FCSTD DOCUMENT  (FreeCAD 0.20R29410 (Git))
Label: co2-sensor-case-v3
License: All rights reserved
LicenseURL: http://en.wikipedia.org/wiki/All_rights_reserved
objects: Part::Extrusion×10, Sketcher::SketchObject×7, Part::Cut×2, Part::Fillet×2, PartDesign::FeatureBase×1, PartDesign::Pocket×1, PartDesign::PolarPattern×1, PartDesign::Body×1, Part::FeaturePython×1
note: 27 computed .brp shape members not serialized (recipe doc carries the construction recipe); baked Part::Feature solids carry a one-line shape summary decoded from their .brp

FEATURE [Sketcher::SketchObject] Sketch
  FullyConstrained = true
  MapMode = 5
  Support = -> [XY_Plane]
  sketch-geometry (2):
    g0: Circle CenterX=0 CenterY=0 CenterZ=0 NormalX=0 NormalY=0 NormalZ=1 AngleXU=0 Radius=20
    g1: Circle CenterX=0 CenterY=0 CenterZ=0 NormalX=0 NormalY=0 NormalZ=1 AngleXU=0 Radius=18
  constraints (4):
    c: Coincident(g0,g-1)
    c: Diameter(g0) = 40
    c: Coincident(g1,g0)
    c: Diameter(g1) = 36
FEATURE [Part::Extrusion] Extrude
  Base = -> Sketch
  Dir = (0,0,1)
  DirMode = 2
  FaceMakerClass = Part::FaceMakerBullseye
  LengthFwd = 70
  LengthRev = 0
  Solid = true
  Symmetric = false
FEATURE [Sketcher::SketchObject] Sketch001
  FullyConstrained = true
  MapMode = 5
  Support = -> [XY_Plane]
  sketch-geometry (1):
    g0: Circle CenterX=0 CenterY=0 CenterZ=0 NormalX=0 NormalY=0 NormalZ=1 AngleXU=0 Radius=18
  constraints (2):
    c: Coincident(g0,g-1)
    c: Diameter(g0) = 36
FEATURE [Part::Extrusion] Extrude001
  Base = -> Sketch001
  Dir = (0,0,1)
  DirMode = 2
  FaceMakerClass = Part::FaceMakerBullseye
  LengthFwd = 2
  LengthRev = 0
  Solid = true
  Symmetric = false
FEATURE [Sketcher::SketchObject] Sketch002
  FullyConstrained = true
  MapMode = 5
  Placement = pos=(0,0,2) rot=(0,0,1;0rad)
  Support = -> [Extrude001]
  sketch-geometry (5):
    g0: LineSegment StartX=-2 StartY=-16.5 StartZ=0 EndX=-2 EndY=16.5 EndZ=0
    g1: LineSegment StartX=-2 StartY=16.5 StartZ=0 EndX=2 EndY=16.5 EndZ=0
    g2: LineSegment StartX=2 StartY=16.5 StartZ=0 EndX=2 EndY=-16.5 EndZ=0
    g3: LineSegment StartX=2 StartY=-16.5 StartZ=0 EndX=-2 EndY=-16.5 EndZ=0
    g4: GeomPoint X=0 Y=0 Z=0
  constraints (12):
    c: Coincident(g0,g1)
    c: Coincident(g1,g2)
    c: Coincident(g2,g3)
    c: Coincident(g3,g0)
    c: Horizontal(g1)
    c: Horizontal(g3)
    c: Vertical(g0)
    c: Vertical(g2)
    c: Symmetric(g1,g0,g4)
    c: Coincident(g4,g-1)
    c: DistanceX(g1,g1) = 4
    c: DistanceY(g2,g2) = 33
FEATURE [Part::Extrusion] Extrude002
  Base = -> Sketch002
  Dir = (0,0,1)
  DirMode = 2
  FaceMakerClass = Part::FaceMakerBullseye
  LengthFwd = 66
  LengthRev = 0
  Solid = true
  Symmetric = false
FEATURE [Sketcher::SketchObject] Sketch003
  FullyConstrained = true
  MapMode = 5
  Placement = pos=(0,0,70) rot=(0,0,1;0rad)
  Support = -> [Extrude]
  sketch-geometry (1):
    g0: Circle CenterX=0 CenterY=0 CenterZ=0 NormalX=0 NormalY=0 NormalZ=1 AngleXU=0 Radius=18
  constraints (2):
    c: Coincident(g0,g-1)
    c: Diameter(g0) = 36
FEATURE [Part::Extrusion] Extrude003
  Base = -> Sketch003
  Dir = (0,0,1)
  DirMode = 2
  FaceMakerClass = Part::FaceMakerBullseye
  LengthFwd = -2
  LengthRev = 0
  Solid = true
  Symmetric = false
FEATURE [Sketcher::SketchObject] Sketch004
  FullyConstrained = true
  MapMode = 5
  Placement = pos=(0,0,0) rot=(0.57735,0.57735,0.57735;2.0944rad)
  Support = -> [YZ_Plane]
  sketch-geometry (4):
    g0: LineSegment StartX=2 StartY=4 StartZ=0 EndX=2 EndY=0 EndZ=0
    g1: LineSegment StartX=2 StartY=0 StartZ=0 EndX=-2 EndY=0 EndZ=0
    g2: LineSegment StartX=-2 StartY=0 StartZ=0 EndX=-2 EndY=4 EndZ=0
    g3: ArcOfCircle CenterX=1e-16 CenterY=4 CenterZ=0 NormalX=0 NormalY=0 NormalZ=1 AngleXU=0 Radius=2 StartAngle=-2.58549e-11 EndAngle=3.14159
  constraints (13):
    c: Coincident(g0,g1)
    c: Coincident(g1,g2)
    c: Horizontal(g1)
    c: Vertical(g0)
    c: Vertical(g2)
    c: PointOnObject(g0,g-1)
    c: DistanceX(g2,g0) = 4
    c: DistanceY(g0,g0) = 4
    c: DistanceX(g1,g-1) = 2
    c: Equal(g0,g2)
    c: Horizontal(g2,g3)
    c: Coincident(g0,g3)
    c: Coincident(g2,g3)
FEATURE [Part::Extrusion] Extrude004
  Base = -> Sketch004
  Dir = (1,-1e-16,1e-16)
  DirMode = 2
  FaceMakerClass = Part::FaceMakerBullseye
  LengthFwd = 40
  LengthRev = 0
  Solid = true
  Symmetric = true
FEATURE [Part::Extrusion] Extrude005
  Base = -> Sketch004
  Dir = (1,-1e-16,1e-16)
  DirMode = 2
  FaceMakerClass = Part::FaceMakerBullseye
  LengthFwd = 40
  LengthRev = 0
  Placement = pos=(10,0,0) rot=(0,0,1;0rad)
  Solid = true
  Symmetric = true
FEATURE [Part::Extrusion] Extrude006
  Base = -> Sketch004
  Dir = (1,-1e-16,1e-16)
  DirMode = 2
  FaceMakerClass = Part::FaceMakerBullseye
  LengthFwd = 30
  LengthRev = 0
  Solid = true
  Symmetric = true
FEATURE [Part::Cut] Cut
  Base = -> Extrude
  Tool = -> Extrude005
FEATURE [Part::Fillet] Fillet
  Base = -> Extrude002
  Edges = 4 edges r=1.9: [Edge1,Edge2,Edge5,Edge8]
FEATURE [Sketcher::SketchObject] Sketch005
  FullyConstrained = true
  MapMode = 5
  Placement = pos=(0,0,0) rot=(0.57735,0.57735,0.57735;2.0944rad)
  Support = -> [YZ_Plane]
  sketch-geometry (8):
    g0: LineSegment StartX=-14.7 StartY=50 StartZ=0 EndX=-12.7 EndY=50 EndZ=0
    g1: LineSegment StartX=-12.7 StartY=50 StartZ=0 EndX=-12.7 EndY=10 EndZ=0
    g2: LineSegment StartX=-12.7 StartY=10 StartZ=0 EndX=-14.7 EndY=10 EndZ=0
    g3: LineSegment StartX=-14.7 StartY=10 StartZ=0 EndX=-14.7 EndY=50 EndZ=0
    g4: LineSegment StartX=12.7 StartY=50 StartZ=0 EndX=14.7 EndY=50 EndZ=0
    g5: LineSegment StartX=14.7 StartY=50 StartZ=0 EndX=14.7 EndY=10 EndZ=0
    g6: LineSegment StartX=14.7 StartY=10 StartZ=0 EndX=12.7 EndY=10 EndZ=0
    g7: LineSegment StartX=12.7 StartY=10 StartZ=0 EndX=12.7 EndY=50 EndZ=0
  constraints (24):
    c: Coincident(g0,g1)
    c: Coincident(g1,g2)
    c: Coincident(g2,g3)
    c: Coincident(g3,g0)
    c: Horizontal(g0)
    c: Horizontal(g2)
    c: Vertical(g1)
    c: Vertical(g3)
    c: Coincident(g4,g5)
    c: Coincident(g5,g6)
    c: Coincident(g6,g7)
    c: Coincident(g7,g4)
    c: Horizontal(g4)
    c: Horizontal(g6)
    c: Vertical(g5)
    c: Vertical(g7)
    c: DistanceX(g0,g0) = 2
    c: DistanceY(g3,g3) = 40
    c: Equal(g3,g5)
    c: DistanceY(g-1,g1) = 10
    c: DistanceY(g1,g6) = 0
    c: DistanceX(g1,g-1) = 12.7
    c: DistanceX(g-1,g6) = 12.7
    c: Equal(g0,g4)
FEATURE [Part::Extrusion] Extrude007
  Base = -> Sketch005
  Dir = (1,-1e-16,1e-16)
  DirMode = 2
  FaceMakerClass = Part::FaceMakerBullseye
  LengthFwd = 16
  LengthRev = 0
  Solid = true
  Symmetric = true
FEATURE [Part::Fillet] Fillet001
  Base = -> Extrude007
  Edges = 8 edges r=0.9: [Edge6,Edge7,Edge11,Edge12,Edge18,Edge19,Edge23,Edge24]
FEATURE [Sketcher::SketchObject] Sketch006
  AttachmentOffset = pos=(0,12,20) rot=(0,0,1;0rad)
  FullyConstrained = true
  MapMode = 5
  Placement = pos=(20,-1.8e-15,12) rot=(0.57735,0.57735,0.57735;2.0944rad)
  Support = -> [YZ_Plane]
  sketch-geometry (27):
    g0: Circle CenterX=0 CenterY=0 CenterZ=0 NormalX=0 NormalY=0 NormalZ=1 AngleXU=0 Radius=1.25
    g1: Circle CenterX=-0.0133326 CenterY=3.99998 CenterZ=0 NormalX=0 NormalY=0 NormalZ=1 AngleXU=0 Radius=1.25
    g2: LineSegment StartX=0 StartY=0 StartZ=0 EndX=-0.0133326 EndY=3.99998 EndZ=0
    g3: Circle CenterX=-0.0266653 CenterY=7.99996 CenterZ=0 NormalX=0 NormalY=0 NormalZ=1 AngleXU=0 Radius=1.25
    g4: LineSegment StartX=-0.0133326 StartY=3.99998 StartZ=0 EndX=-0.0266653 EndY=7.99996 EndZ=0
    g5: Circle CenterX=-0.0399979 CenterY=11.9999 CenterZ=0 NormalX=0 NormalY=0 NormalZ=1 AngleXU=0 Radius=1.25
    g6: LineSegment StartX=-0.0266653 StartY=7.99996 StartZ=0 EndX=-0.0399979 EndY=11.9999 EndZ=0
    g7: Circle CenterX=-0.0533306 CenterY=15.9999 CenterZ=0 NormalX=0 NormalY=0 NormalZ=1 AngleXU=0 Radius=1.25
    g8: LineSegment StartX=-0.0399979 StartY=11.9999 StartZ=0 EndX=-0.0533306 EndY=15.9999 EndZ=0
    g9: Circle CenterX=-0.0666632 CenterY=19.9999 CenterZ=0 NormalX=0 NormalY=0 NormalZ=1 AngleXU=0 Radius=1.25
    g10: LineSegment StartX=-0.0533306 StartY=15.9999 StartZ=0 EndX=-0.0666632 EndY=19.9999 EndZ=0
    g11: Circle CenterX=-0.0799958 CenterY=23.9999 CenterZ=0 NormalX=0 NormalY=0 NormalZ=1 AngleXU=0 Radius=1.25
    g12: LineSegment StartX=-0.0666632 StartY=19.9999 StartZ=0 EndX=-0.0799958 EndY=23.9999 EndZ=0
    g13: Circle CenterX=-0.0933285 CenterY=27.9998 CenterZ=0 NormalX=0 NormalY=0 NormalZ=1 AngleXU=0 Radius=1.25
    g14: LineSegment StartX=-0.0799958 StartY=23.9999 StartZ=0 EndX=-0.0933285 EndY=27.9998 EndZ=0
    g15: Circle CenterX=-0.106661 CenterY=31.9998 CenterZ=0 NormalX=0 NormalY=0 NormalZ=1 AngleXU=0 Radius=1.25
    g16: LineSegment StartX=-0.0933285 StartY=27.9998 StartZ=0 EndX=-0.106661 EndY=31.9998 EndZ=0
    g17: Circle CenterX=-0.119994 CenterY=35.9998 CenterZ=0 NormalX=0 NormalY=0 NormalZ=1 AngleXU=0 Radius=1.25
    g18: LineSegment StartX=-0.106661 StartY=31.9998 StartZ=0 EndX=-0.119994 EndY=35.9998 EndZ=0
    g19: Circle CenterX=-0.133326 CenterY=39.9998 CenterZ=0 NormalX=0 NormalY=0 NormalZ=1 AngleXU=0 Radius=1.25
    g20: LineSegment StartX=-0.119994 StartY=35.9998 StartZ=0 EndX=-0.133326 EndY=39.9998 EndZ=0
    g21: Circle CenterX=-0.146659 CenterY=43.9998 CenterZ=0 NormalX=0 NormalY=0 NormalZ=1 AngleXU=0 Radius=1.25
    g22: LineSegment StartX=-0.133326 StartY=39.9998 StartZ=0 EndX=-0.146659 EndY=43.9998 EndZ=0
    g23: Circle CenterX=-0.159992 CenterY=47.9997 CenterZ=0 NormalX=0 NormalY=0 NormalZ=1 AngleXU=0 Radius=1.25
    g24: LineSegment StartX=-0.146659 StartY=43.9998 StartZ=0 EndX=-0.159992 EndY=47.9997 EndZ=0
    g25: Circle CenterX=-0.173324 CenterY=51.9997 CenterZ=0 NormalX=0 NormalY=0 NormalZ=1 AngleXU=0 Radius=1.25
    g26: LineSegment StartX=-0.159992 StartY=47.9997 StartZ=0 EndX=-0.173324 EndY=51.9997 EndZ=0
  constraints (67):
    c: Coincident(g0,g-1)
    c: Diameter(g0) = 2.5
    c: Equal(g0,g1) = 2
    c: Coincident(g0,g2)
    c: Coincident(g1,g2)
    c: Distance(g2) = 4
    c: Angle(g2) = 1.57413
    c: Equal(g0,g3) = 2
    c: Coincident(g1,g4)
    c: Coincident(g3,g4)
    c: Equal(g2,g4)
    c: Parallel(g4,g2)
    c: Equal(g0,g5) = 2
    c: Coincident(g3,g6)
    c: Coincident(g5,g6)
    c: Equal(g2,g6)
    c: Parallel(g6,g2)
    c: Equal(g0,g7) = 2
    c: Coincident(g5,g8)
    c: Coincident(g7,g8)
    c: Equal(g2,g8)
    c: Parallel(g8,g2)
    c: Equal(g0,g9) = 2
    c: Coincident(g7,g10)
    c: Coincident(g9,g10)
    c: Equal(g2,g10)
    c: Parallel(g10,g2)
    c: Equal(g0,g11) = 2
    c: Coincident(g9,g12)
    c: Coincident(g11,g12)
    c: Equal(g2,g12)
    c: Parallel(g12,g2)
    c: Equal(g0,g13) = 2
    c: Coincident(g11,g14)
    c: Coincident(g13,g14)
    c: Equal(g2,g14)
    c: Parallel(g14,g2)
    c: Equal(g0,g15) = 2
    c: Coincident(g13,g16)
    c: Coincident(g15,g16)
    c: Equal(g2,g16)
    c: Parallel(g16,g2)
    c: Equal(g0,g17) = 2
    c: Coincident(g15,g18)
    c: Coincident(g17,g18)
    c: Equal(g2,g18)
    c: Parallel(g18,g2)
    c: Equal(g0,g19) = 2
    c: Coincident(g17,g20)
    c: Coincident(g19,g20)
    c: Equal(g2,g20)
    c: Parallel(g20,g2)
    c: Equal(g0,g21) = 2
    c: Coincident(g19,g22)
    c: Coincident(g21,g22)
    c: Equal(g2,g22)
    c: Parallel(g22,g2)
    c: Equal(g0,g23) = 2
    c: Coincident(g21,g24)
    c: Coincident(g23,g24)
    c: Equal(g2,g24)
    c: Parallel(g24,g2)
    c: Equal(g0,g25) = 2
    c: Coincident(g23,g26)
    c: Coincident(g25,g26)
    c: Equal(g2,g26)
    c: Parallel(g26,g2)
FEATURE [Part::Extrusion] Extrude008
  Base = -> Sketch006
  Dir = (1,-1e-16,1e-16)
  DirMode = 2
  FaceMakerClass = Part::FaceMakerBullseye
  LengthFwd = -2
  LengthRev = 0
  Solid = true
  Symmetric = false
FEATURE [Part::Cut] Cut001
  Base = -> Cut
  Tool = -> Extrude008
FEATURE [PartDesign::FeatureBase] BaseFeature
  BaseFeature = -> Cut
FEATURE [Part::Extrusion] Extrude009
  Base = -> Sketch006
  Dir = (1,-1e-16,1e-16)
  DirMode = 2
  FaceMakerClass = Part::FaceMakerBullseye
  LengthFwd = -2
  LengthRev = 0
  Solid = true
  Symmetric = false
FEATURE [PartDesign::Pocket] Pocket
  BaseFeature = -> BaseFeature
  Direction = (-1,2e-16,-3e-16)
  Length = 4
  Length2 = 5
  Profile = -> Sketch006
  ReferenceAxis = -> Sketch006 [N_Axis]
  Type = 0
FEATURE [PartDesign::PolarPattern] PolarPattern
  Angle = 360
  Axis = -> Z_Axis
  BaseFeature = -> Pocket
  Occurrences = 36
  Originals = -> [Pocket]
  Reversed = true
FEATURE [PartDesign::Body] Body
  BaseFeature = -> Cut
  Group = -> [BaseFeature,Sketch,Sketch001,Sketch002,Sketch003,Sketch004,Sketch005,Sketch006,Pocket,PolarPattern]
  Origin = -> Origin
  Tip = -> PolarPattern
FEATURE [Part::FeaturePython] Connect  # WARN: FeaturePython — macro-defined, semantics opaque (R4)
  Objects = -> [PolarPattern,Extrude003]
  Tolerance = 0
